# Revit family: PLB_ep140_R3.85
name_source: partatom
category: Equipement spécialisé
revit_build: Autodesk Revit Architecture 2016 (Build: 20150220_1215(x64)
units: mm (PartAtom-declared; Revit-internal decimal feet)

## family parameters
Basée sur le plan de construction = Non
Cote de connecteur circulaire = Utiliser le diamètre
Couper avec des vides une fois chargée = Non
Partagée = Non
Point de calcul de pièce = Non
Toujours verticalement = Oui
Type d'élément = Normal

## types (1)
- PLB_ep140_R3.85
    Absorption d'eau à court terme par immersion partielle = WS
    Conductivité thermique = 0.0360 W/(m·K)
    Contrainte en compression pour 10% de déformation = CS(10)30
    Coût = 0 $
    Description = Eticsbox épaisseur 140
    Empreinte carbone = Kg CO2 eq/m²
    Fabricant = Isobox
    Image du type = bande_plb.jpg
    Masse volumique nominale = 90.00 kg/m³
    Matériaux = Isolant Laine minérale
    Modèle = ep : 140mm
    Réaction au feu = Euroclasse A1
    Résistance thermique = 3.8500 (m²·K)/W
    Résistance à la traction perpendiculaire au faces = TR10
    URL = http://www.isobox-isolation.fr

## geometry (parser evidence)
native form markers: Blend x12
no freeform markers — native parametric forms only
